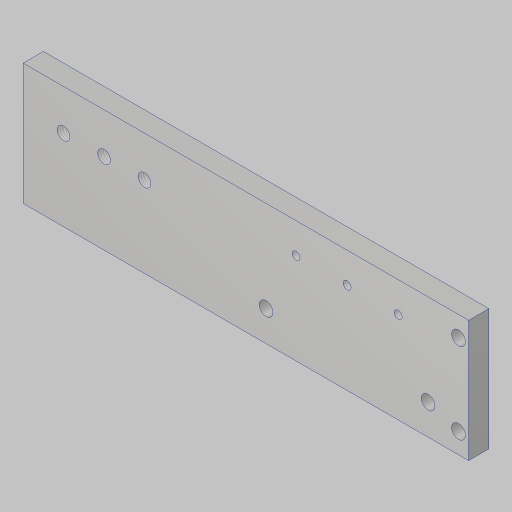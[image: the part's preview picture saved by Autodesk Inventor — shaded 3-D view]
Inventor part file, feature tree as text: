
AUTODESK INVENTOR PART (.ipt)
format: ipt  version: 2023.5 (Build 275446000, 446)  size: 148,480 bytes
history: native  units: in
note: dims shown in document units (in); Inventor stores cm internally (conversion verified against a paired STEP export)
features: sketch x4, hole x3, extrude x1
ambient origin geometry x8: Origin, YZ Plane, XZ Plane, XY Plane, X Axis, Y Axis, Z Axis, Center Point
bodies: Solid1 (feature_tree)
feature tree (8):
  extrude  "Extrusion1"  Depth=1.5in
  hole  "Hole1"  [1 undecoded]
  hole  "Hole2"  [1 undecoded]
  hole  "Hole3"  [1 undecoded]
  sketch  "Sketch1"  dims[d0=5.5in d1=1.5in]
  sketch  "Sketch2"  dims[d2=0.25in d3=0.0in d4=0.5in d5=0.5in]
  sketch  "Sketch3"  dims[d6=0.5in]
  sketch  "Sketch6"  dims[d7=0.156in d8=0.38in d9=0.385in d10=0.25in d11=0.5635in d12=1.0in d13=0.8108in d14=0.5in d15=0.5in d16=0.25in d17=0.25in d18=0.125in d19=0.17in d20=0.328in d21=0.332in d22=0.25in d23=0.5635in d24=1.0in d25=0.8108in d30=1.2598in d32=0.0968in d33=0.236in d34=0.385in d35=0.25in d36=0.5635in d37=1.0in d38=0.8108in d39=2.0in d41=1.125in d43=0.5in d45=1.125in d46=1.5in d47=0.315in]
note: 3 required parameter values undecoded (feature->parameter linkage not recoverable at this tier; creation-order binding heuristic only, values carry confidence <= 0.55)
